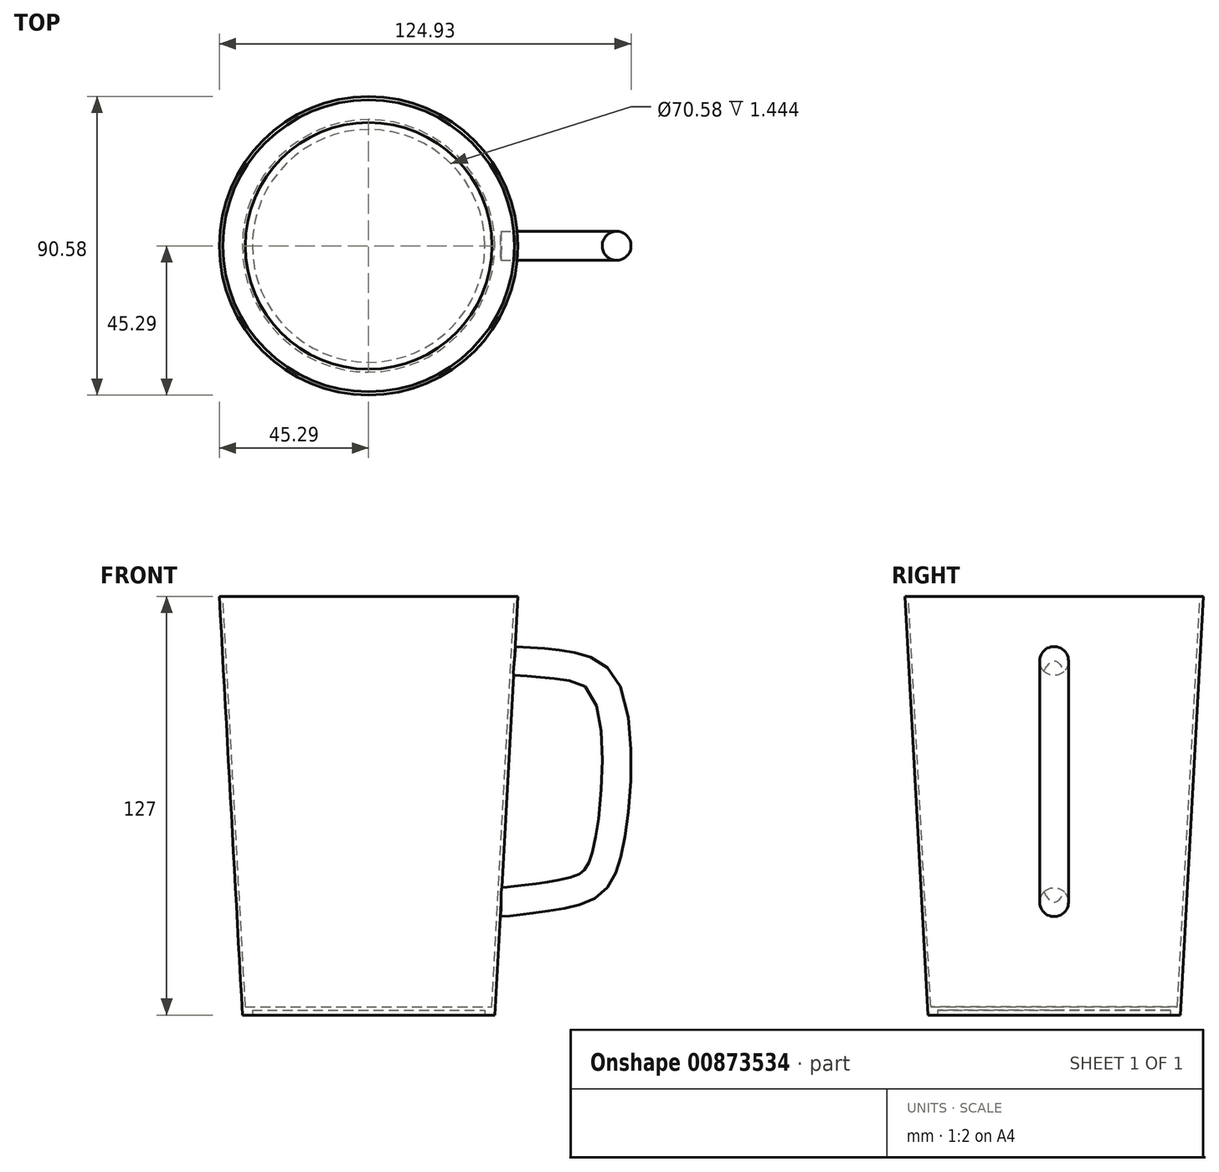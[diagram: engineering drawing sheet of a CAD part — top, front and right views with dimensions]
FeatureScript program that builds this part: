
annotation { "Feature Type Name" : "Feature", "Feature Type Description" : "" }
export const myFeature = defineFeature(function(context is Context, id is Id, definition is map)
    precondition{}
    {
        {
            var Q0;
            Q0=qCreatedBy(makeId("Front.planeOp"),FACE);
            var sketch = newSketch(context, id + "F0", { "sketchPlane" : qUnion([Q0])});
            skLineSegment(sketch, "E0", {"start": v(45.29, 125.56) * mm, "end": v(38.3, -1.44) * mm});
            skLineSegment(sketch, "E1.0", {"start": v(44.27, 125.56) * mm, "end": v(37.41, 1.06) * mm});
            skLineSegment(sketch, "E2", {"start": v(45.29, 125.56) * mm, "end": v(44.27, 125.56) * mm});
            skLineSegment(sketch, "E3", {"start": v(0, 0) * mm, "end": v(0, 139.55) * mm});
            skFitSpline(sketch, "E4", {"points": [v(44.2, 105.95) * mm, v(59.22, 104.65) * mm, v(69.94, 100.32) * mm, v(75.2, 79.26) * mm, v(71.07, 43.7) * mm, v(63.36, 36.37) * mm, v(45.3, 33.36) * mm, v(40.18, 32.8) * mm], "startDerivative": vector(103.76, -5.9) * mm, "endDerivative": vector(-64.58, -0.97) * mm});
            skFitSpline(sketch, "E5.0", {"points": [v(43.85, 99.6) * mm, v(44.92, 99.55) * mm, v(47.1, 99.42) * mm, v(49.87, 99.23) * mm, v(52.07, 99.06) * mm, v(53.43, 98.93) * mm, v(54.5, 98.83) * mm, v(55.3, 98.74) * mm, v(56.09, 98.65) * mm, v(56.74, 98.57) * mm, v(57.25, 98.5) * mm, v(57.63, 98.46) * mm, v(57.95, 98.42) * mm, v(58.2, 98.38) * mm, v(58.45, 98.34) * mm, v(58.76, 98.3) * mm, v(59.24, 98.23) * mm, v(59.82, 98.13) * mm, v(60.47, 98.01) * mm, v(61.1, 97.89) * mm, v(61.67, 97.75) * mm, v(62.39, 97.56) * mm, v(63.17, 97.31) * mm, v(63.8, 97.04) * mm, v(64.23, 96.82) * mm, v(64.5, 96.65) * mm, v(64.75, 96.48) * mm, v(64.94, 96.34) * mm, v(65.07, 96.21) * mm, v(65.17, 96.12) * mm, v(65.26, 96.04) * mm, v(65.32, 95.97) * mm, v(65.38, 95.9) * mm, v(65.47, 95.8) * mm, v(65.6, 95.62) * mm, v(65.79, 95.37) * mm, v(66.02, 95) * mm, v(66.25, 94.58) * mm, v(66.48, 94.1) * mm, v(66.8, 93.37) * mm, v(67.17, 92.31) * mm, v(67.59, 90.81) * mm, v(67.95, 89.1) * mm, v(68.26, 87.2) * mm, v(68.5, 85.12) * mm, v(68.66, 83.25) * mm, v(68.76, 81.68) * mm, v(68.82, 80.47) * mm, v(68.86, 79.23) * mm, v(68.9, 77.53) * mm, v(68.91, 75.33) * mm, v(68.88, 72.63) * mm, v(68.8, 69.88) * mm, v(68.6, 66.2) * mm, v(68.31, 62.54) * mm, v(67.92, 59.01) * mm, v(67.58, 56.47) * mm, v(67.2, 54.06) * mm, v(66.77, 51.81) * mm, v(66.31, 49.76) * mm, v(65.9, 48.25) * mm, v(65.57, 47.19) * mm, v(65.33, 46.47) * mm, v(65.09, 45.83) * mm, v(64.86, 45.29) * mm, v(64.64, 44.84) * mm, v(64.44, 44.47) * mm, v(64.25, 44.18) * mm, v(64.09, 43.95) * mm, v(63.94, 43.77) * mm, v(63.8, 43.62) * mm, v(63.65, 43.49) * mm, v(63.48, 43.36) * mm, v(63.28, 43.22) * mm, v(63.03, 43.07) * mm, v(62.7, 42.91) * mm, v(62.31, 42.74) * mm, v(61.84, 42.56) * mm, v(61.28, 42.37) * mm, v(60.64, 42.18) * mm, v(59.68, 41.92) * mm, v(58.34, 41.61) * mm, v(56.56, 41.27) * mm, v(54.68, 40.95) * mm, v(52.75, 40.67) * mm, v(50.83, 40.42) * mm, v(49.28, 40.23) * mm, v(48.08, 40.09) * mm, v(47.22, 39.99) * mm, v(46.4, 39.9) * mm, v(45.74, 39.81) * mm, v(45.23, 39.75) * mm, v(44.93, 39.71) * mm, v(44.69, 39.68) * mm, v(44.5, 39.66) * mm, v(44.33, 39.64) * mm, v(44.1, 39.6) * mm, v(43.84, 39.57) * mm, v(43.43, 39.52) * mm, v(42.96, 39.45) * mm, v(42.47, 39.38) * mm, v(42.03, 39.32) * mm, v(41.65, 39.27) * mm, v(41.32, 39.23) * mm, v(41.02, 39.2) * mm, v(40.72, 39.18) * mm, v(40.42, 39.16) * mm, v(40.2, 39.16) * mm, v(40.09, 39.16) * mm]});
            skLineSegment(sketch, "E6.bottom", {"start": v(0, 0) * mm, "end": v(35.29, 0) * mm});
            skLineSegment(sketch, "E6.top", {"start": v(0, 1.06) * mm, "end": v(37.41, 1.06) * mm});
            skLineSegment(sketch, "E6.left", {"start": v(0, 0) * mm, "end": v(0, 1.06) * mm});
            skLineSegment(sketch, "E7", {"start": v(38.3, -1.44) * mm, "end": v(35.29, -1.44) * mm});
            skLineSegment(sketch, "E8", {"start": v(35.29, -1.44) * mm, "end": v(35.29, 0) * mm});
            skPoint(sketch, "E9.orphan", {"position": v(38.37, 0) * mm});
            skSolve(sketch);
        }
        {
            var Q0;
            Q0=makeQuery(id+"F0.imprint","IMPRINT",FACE,{"disambiguationData":[TD([[makeQuery(id+"F0.imprint","IMPRINT",EDGE,{"derivedFrom":sQuery(id+"F0.wireOp",EDGE,"E0")}),-1.0]])]});
            var Q1;
            Q1=sQuery(id+"F0.wireOp",EDGE,"E3");
            revolve(context, id + "F1", {"surfaceOperationType" : NewSurfaceOperationType.NEW, "entities" : qUnion([Q0]), "axis" : qUnion([Q1]), "revolveType" : RevolveType.FULL});
        }
        {
            var Q0;
            Q0=qCreatedBy(makeId("Top.planeOp"),FACE);
            cPlane(context, id + "F2", {"entities" : qUnion([Q0]), "cplaneType" : CPlaneType.OFFSET, "offset" : 79.76 * mm, "width" : 152.4 * mm, "height" : 152.4 * mm});
        }
        {
            var Q0;
            Q0=qCreatedBy(id+"F2.planeOp",FACE);
            var sketch = newSketch(context, id + "F3", { "sketchPlane" : qUnion([Q0])});
            skLineSegment(sketch, "E10", {"start": v(68.84, 0) * mm, "end": v(75.2, 0) * mm, "construction": true});
            skCircle(sketch, "E11", {"center": v(75.2, 0) * mm, "radius": 4.39 * mm});
            skSolve(sketch);
        }
        {
            var Q0;
            Q0=makeQuery(id+"F3.imprint","IMPRINT",FACE,{"disambiguationData":[TD([[makeQuery(id+"F3.imprint","IMPRINT",EDGE,{"derivedFrom":sQuery(id+"F3.wireOp",EDGE,"E11")}),1.0]])]});
            var Q1;
            Q1=sQuery(id+"F0.wireOp",EDGE,"E4");
            sweep(context, id + "F4", {"operationType" : NewBodyOperationType.ADD, "profiles" : qUnion([Q0]), "path" : qUnion([Q1])});
        }
    });
